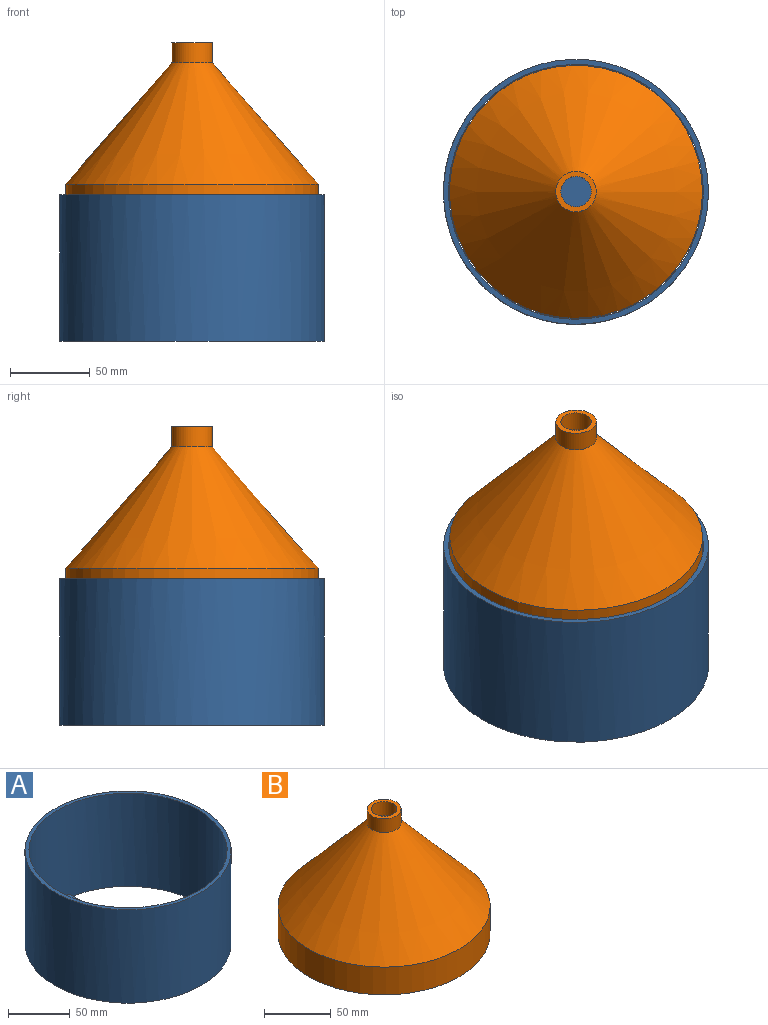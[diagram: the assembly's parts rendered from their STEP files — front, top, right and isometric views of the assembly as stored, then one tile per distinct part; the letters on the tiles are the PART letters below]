
ASSEMBLY  parts=2 mates=1
PART A: 10 faces, bbox 166.4x166.4x92.1 mm
  f0: plane 166.37x166.37mm, normal (0,0,-1), area 5603mm2, adj f1,f2,f4,f5,f7,f8,f9
  f1: cylinder r=80.01mm len=160.02mm, axis (0,0,1), area 46125.8mm2, adj f0,f3,f4,f5,f6
  f2: cylinder r=83.18mm len=166.37mm, axis (0,0,1), area 48124.5mm2, adj f0,f3
  f3: plane 166.37x166.37mm, normal (0,0,1), area 1627.8mm2, adj f1,f2
  f4: plane 157.99x3.18mm, normal (-1,0,0), area 501.6mm2, adj f0,f1,f6
  f5: plane 157.99x3.18mm, normal (1,0,0), area 501.6mm2, adj f0,f1,f6
  f6: plane 160.02x25.4mm, normal (0,0,1), area 3975.2mm2, adj f1,f4,f5,f7,f8,f9
  f7: cylinder r=3.17mm len=6.35mm, axis (0,0,-1), area 63.3mm2, adj f0,f6
  f8: cylinder r=2.54mm len=5.08mm, axis (0,0,-1), area 50.7mm2, adj f0,f6
  f9: cylinder r=2.54mm len=5.08mm, axis (0,0,-1), area 50.7mm2, adj f0,f6
PART B: 8 faces, bbox 158.8x158.8x114.3 mm
  f0: cylinder r=76.2mm len=152.4mm, axis (0,0,-1), area 12161mm2, adj f2,f4
  f1: cylinder r=79.38mm len=158.75mm, axis (0,0,-1), area 12667.7mm2, adj f2,f3
  f2: plane 158.75x158.75mm, normal (0,0,-1), area 1551.8mm2, adj f0,f1
  f3: cone r=79.38mm half-angle=41.2deg, axis (0,0,-1), area 29288.4mm2, adj f1,f6
  f4: cone r=9.53mm half-angle=41.2deg, axis (0,0,-1), area 27268.5mm2, adj f0,f5
  f5: cylinder r=9.53mm len=19.05mm, axis (0,0,-1), area 760.1mm2, adj f4,f7
  f6: cylinder r=12.7mm len=25.4mm, axis (0,0,-1), area 1013.4mm2, adj f3,f7
  f7: plane 25.4x25.4mm, normal (0,0,1), area 221.7mm2, adj f5,f6
PLACE A t=(276.18,-117.67,73.76)mm
PLACE B t=(276.18,-117.67,99.42)mm
MATE cylindrical B.f1 <-> A.f1  axis (0,0,-1) through (276.18,-117.67,99.42)mm
